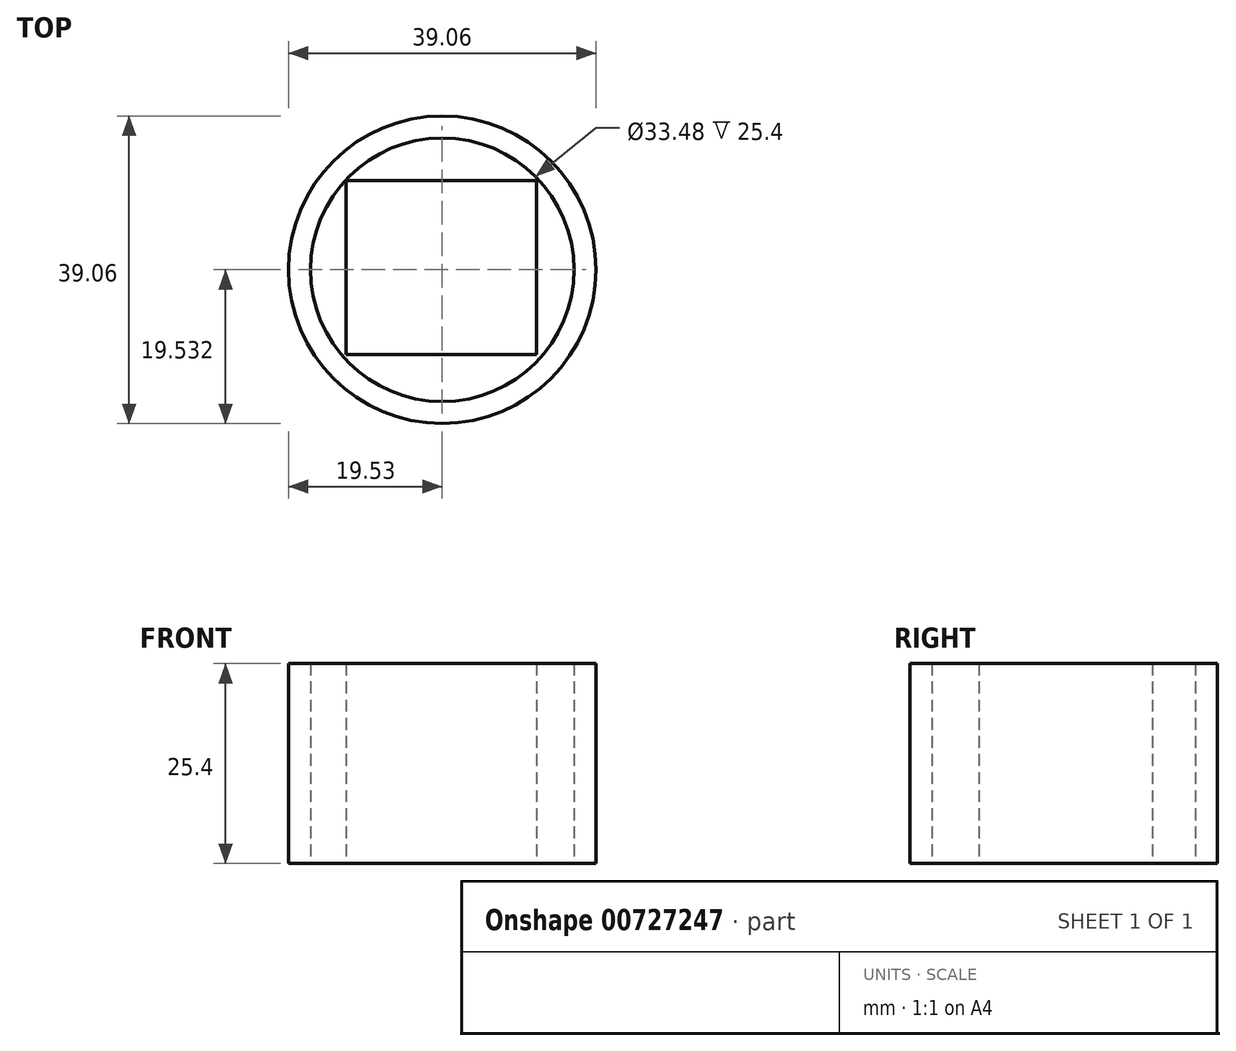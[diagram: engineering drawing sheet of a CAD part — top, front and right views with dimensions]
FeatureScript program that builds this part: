
annotation { "Feature Type Name" : "Feature", "Feature Type Description" : "" }
export const myFeature = defineFeature(function(context is Context, id is Id, definition is map)
    precondition{}
    {
        {
            var Q0;
            Q0=qCreatedBy(makeId("Top.planeOp"),FACE);
            var sketch = newSketch(context, id + "F0", { "sketchPlane" : qUnion([Q0])});
            skCircle(sketch, "E0", {"center": v(-43.74, 22.3) * mm, "radius": 19.53 * mm});
            skCircle(sketch, "E1", {"center": v(-43.74, 22.3) * mm, "radius": 16.74 * mm});
            skSolve(sketch);
        }
        {
            var Q0;
            Q0=makeQuery(id+"F0.imprint","IMPRINT",FACE,{"disambiguationData":[TD([[makeQuery(id+"F0.imprint","IMPRINT",EDGE,{"derivedFrom":sQuery(id+"F0.wireOp",EDGE,"E0")}),1.0]])]});
            extrude(context, id + "F1", {"entities" : qUnion([Q0]), "depth" : 25.4 * mm, "offsetDistance" : 25.4 * mm});
        }
        {
            var Q0;
            Q0=qCreatedBy(makeId("Top.planeOp"),FACE);
            var sketch = newSketch(context, id + "F2", { "sketchPlane" : qUnion([Q0])});
            skLineSegment(sketch, "E2.bottom", {"start": v(-55.98, 33.6) * mm, "end": v(-31.76, 33.6) * mm});
            skLineSegment(sketch, "E2.top", {"start": v(-55.98, 11.52) * mm, "end": v(-31.76, 11.52) * mm});
            skLineSegment(sketch, "E2.left", {"start": v(-55.98, 33.6) * mm, "end": v(-55.98, 11.52) * mm});
            skLineSegment(sketch, "E2.right", {"start": v(-31.76, 33.6) * mm, "end": v(-31.76, 11.52) * mm});
            skSolve(sketch);
        }
        {
            var Q0;
            Q0=makeQuery(id+"F2.imprint","IMPRINT",FACE,{"disambiguationData":[TD([[makeQuery(id+"F2.imprint","IMPRINT",EDGE,{"derivedFrom":sQuery(id+"F2.wireOp",EDGE,"E2.bottom")}),-1.0]])]});
            extrude(context, id + "F3", {"entities" : qUnion([Q0]), "depth" : 25.4 * mm, "offsetDistance" : 25.4 * mm});
        }
    });
